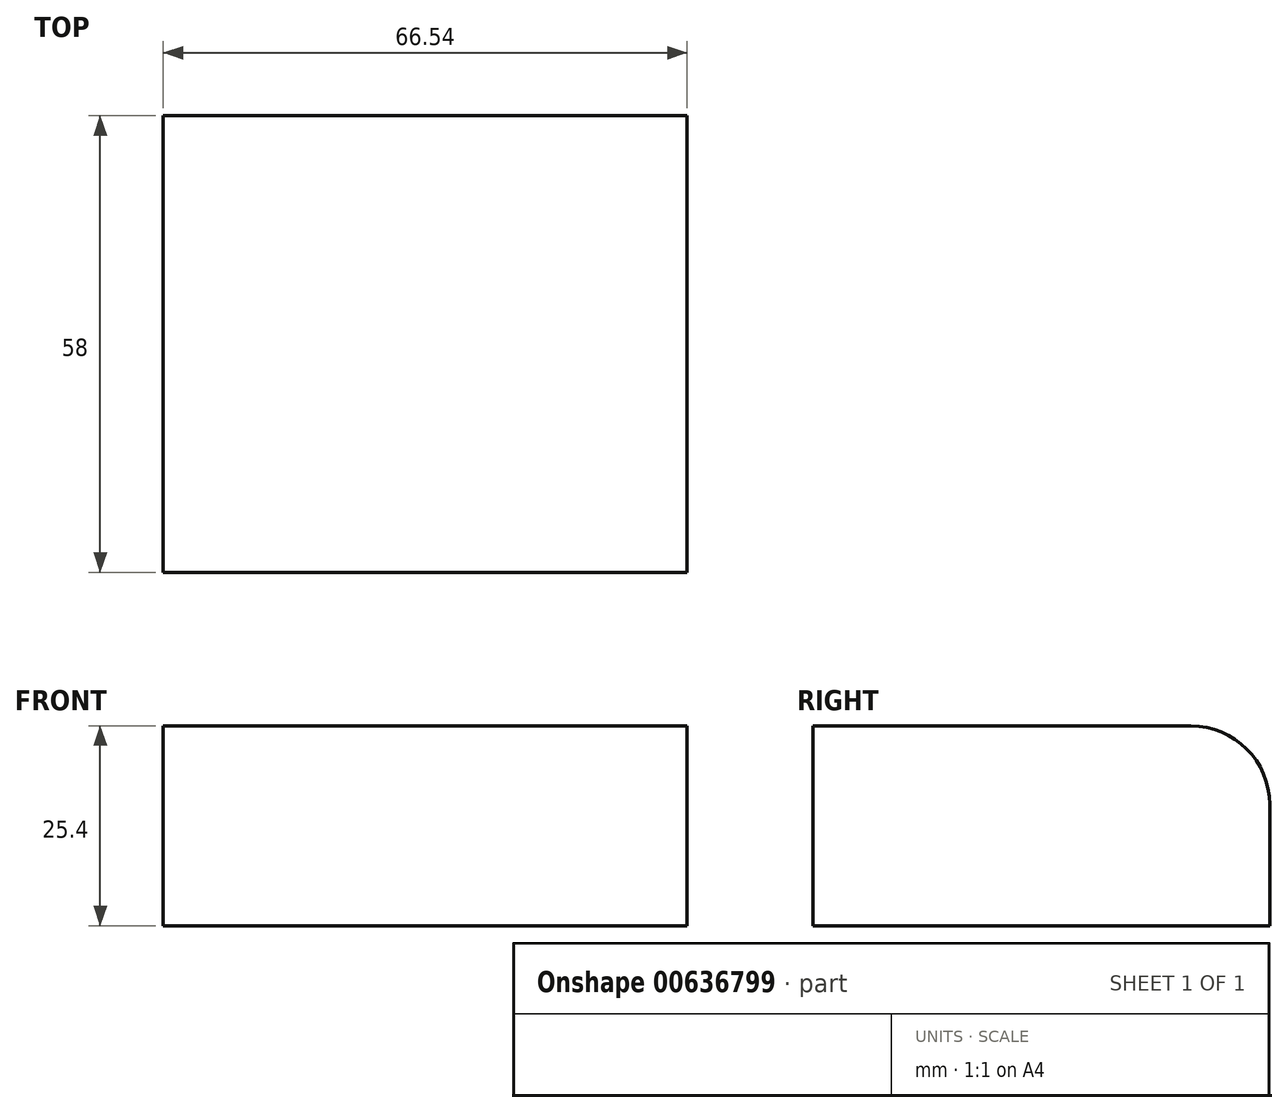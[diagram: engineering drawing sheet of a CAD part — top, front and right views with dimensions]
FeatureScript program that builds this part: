
annotation { "Feature Type Name" : "Feature", "Feature Type Description" : "" }
export const myFeature = defineFeature(function(context is Context, id is Id, definition is map)
    precondition{}
    {
        {
            var Q0;
            Q0=qCreatedBy(makeId("Top.planeOp"),FACE);
            var sketch = newSketch(context, id + "F0", { "sketchPlane" : qUnion([Q0])});
            skLineSegment(sketch, "E0.bottom", {"start": v(-36.34, 33.78) * mm, "end": v(30.2, 33.78) * mm});
            skLineSegment(sketch, "E0.top", {"start": v(-36.34, -24.22) * mm, "end": v(30.2, -24.22) * mm});
            skLineSegment(sketch, "E0.left", {"start": v(-36.34, 33.78) * mm, "end": v(-36.34, -24.22) * mm});
            skLineSegment(sketch, "E0.right", {"start": v(30.2, 33.78) * mm, "end": v(30.2, -24.22) * mm});
            skSolve(sketch);
        }
        {
            var Q0;
            Q0 = qSketchRegion(id + "F0", true);
            var Q1;
            Q1=makeQuery(id+"F0.imprint","IMPRINT",FACE,{"disambiguationData":[TD([[makeQuery(id+"F0.imprint","IMPRINT",EDGE,{"derivedFrom":sQuery(id+"F0.wireOp",EDGE,"E0.bottom")}),-1.0]])]});
            extrude(context, id + "F1", {"entities" : qUnion([Q0, Q1]), "depth" : 25.4 * mm, "offsetDistance" : 25.4 * mm});
        }
        {
            var Q0;
            Q0=makeQuery(id+"F1.opExtrude","CAP_EDGE",EDGE,{"disambiguationData":[OSD([sQuery(id+"F0.wireOp",EDGE,"E0.bottom")])],"isStart":false});
            fillet(context, id + "F2", {"entities" : qUnion([Q0]), "radius" : 10 * mm, "tangentPropagation" : true, "allowEdgeOverflow" : false});
        }
    });
